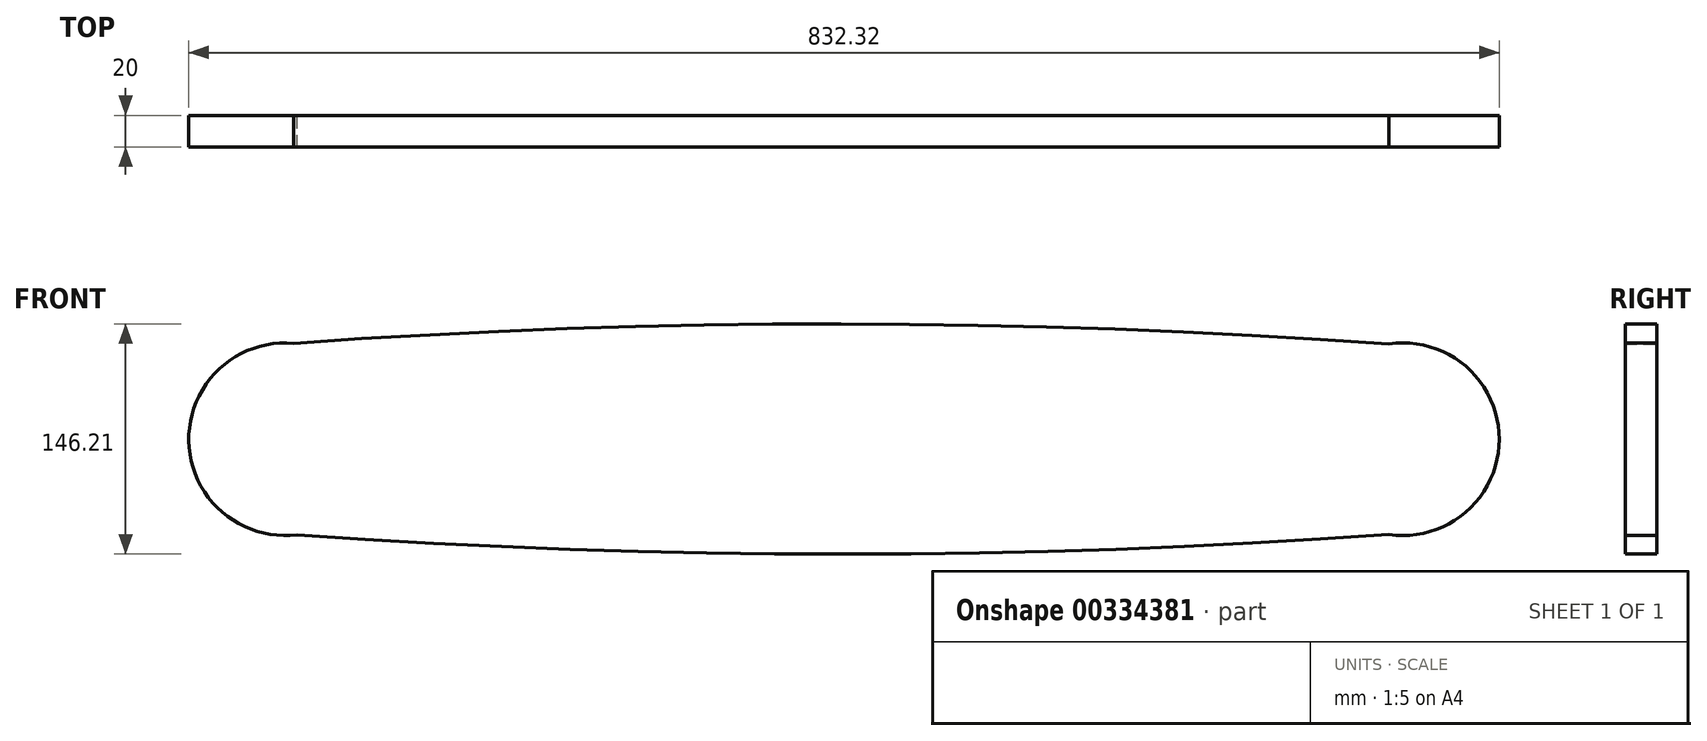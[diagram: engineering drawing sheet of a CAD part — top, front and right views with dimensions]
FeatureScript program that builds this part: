
annotation { "Feature Type Name" : "Feature", "Feature Type Description" : "" }
export const myFeature = defineFeature(function(context is Context, id is Id, definition is map)
    precondition{}
    {
        {
            var Q0;
            Q0=qCreatedBy(makeId("Front.planeOp"),FACE);
            var sketch = newSketch(context, id + "F0", { "sketchPlane" : qUnion([Q0])});
            skCircle(sketch, "E0", {"center": v(-50.35, 0) * mm, "radius": 61.16 * mm});
            skCircle(sketch, "E1", {"center": v(659.65, 0) * mm, "radius": 61.16 * mm});
            skLineSegment(sketch, "E2", {"start": v(-50.35, 0) * mm, "end": v(659.65, 0) * mm});
            skArc(sketch, "E3", {"start": v(-42.75, -60.69) * mm, "mid": v(303.95, -73) * mm, "end": v(650.65, -60.5) * mm});
            skArc(sketch, "E4", {"start": v(650.67, 60.5) * mm, "mid": v(302.82, 73.2) * mm, "end": v(-45.05, 60.93) * mm});
            skSolve(sketch);
        }
        {
            var Q0;
            {var subQ0=sQuery(id+"F0.wireOp",EDGE,"E4");Q0=makeQuery(id+"F0.imprint","IMPRINT",FACE,{"disambiguationData":[TD([[makeQuery(id+"F0.imprint","IMPRINT",EDGE,{"derivedFrom":subQ0}),1.0]])]});}
            var Q1;
            {var subQ0=sQuery(id+"F0.wireOp",EDGE,"E0");var subQ1=makeQuery(id+"F0.imprint","INTERSECT",VERTEX,{"derivedFrom":[subQ0,sQuery(id+"F0.wireOp",EDGE,"E4")]});Q1=makeQuery(id+"F0.imprint","IMPRINT",FACE,{"disambiguationData":[TD([[makeQuery(id+"F0.imprint","IMPRINT",EDGE,{"disambiguationData":[TD([[subQ1,1.0]])],"derivedFrom":subQ0}),1.0]])]});}
            var Q2;
            {var subQ0=sQuery(id+"F0.wireOp",EDGE,"E3");Q2=makeQuery(id+"F0.imprint","IMPRINT",FACE,{"disambiguationData":[TD([[makeQuery(id+"F0.imprint","IMPRINT",EDGE,{"derivedFrom":subQ0}),1.0]])]});}
            var Q3;
            {var subQ0=sQuery(id+"F0.wireOp",EDGE,"E1");var subQ1=makeQuery(id+"F0.imprint","INTERSECT",VERTEX,{"derivedFrom":[subQ0,sQuery(id+"F0.wireOp",EDGE,"E4")]});Q3=makeQuery(id+"F0.imprint","IMPRINT",FACE,{"disambiguationData":[TD([[makeQuery(id+"F0.imprint","IMPRINT",EDGE,{"disambiguationData":[TD([[subQ1,-1.0]])],"derivedFrom":subQ0}),1.0]])]});}
            extrude(context, id + "F1", {"entities" : qUnion([Q0, Q1, Q2, Q3]), "depth" : 20 * mm});
        }
    });
